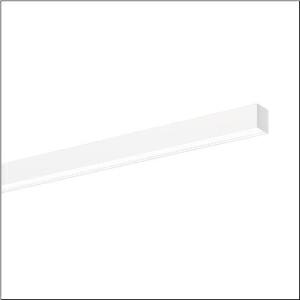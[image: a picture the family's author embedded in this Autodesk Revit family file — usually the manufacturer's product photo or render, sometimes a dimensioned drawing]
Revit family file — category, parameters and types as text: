
# Revit family: silica_r__21_51mx20da32wb_d50a
name_source: partatom
category: Lighting Fixtures
units: mm (PartAtom-declared; Revit-internal decimal feet)

## family parameters
Cut with Voids When Loaded = No
Host = Face
Light Source = No
Part Type = Normal
Room Calculation Point = No
Round Connector Dimension = Use Diameter
Shared = No

## types (1)
- --- (1 x LED, 2400 lm, 16.1 W, 3000K)
    Apparent Load = 16 VA
    CIE Flux Codes = 48 79 96 100 100
    Color Rendering = 80
    Color Temperature = 3000K
    Default Elevation = 1800 mm
    Description = Silica® 21, office luminaire, primary optical cover: cover, of PMMA, opal, light emission: direct distribution, primary light characteristic: symmetric, installation type: surface-mounted, LED, rated luminous flux: 2.400lm, luminous efficacy: 149lm/W, light colour: 830, colour temperature: 3000K, with terminal, 3+2-pole, max. 2.5mm², mains connection: 220..240V, AC, 50/60Hz, rated input power: 16.1W, luminaire housing, of aluminium, traffic white (RAL 9016), length: 1.204mm, width: 53mm, height: 53mm, protection rating (complete): IP20, insulation class (complete): insulation class I (protective earthing), certification: CE, permissible operating ambient temperature: 0..+35°C, standard: EN 50419, packaging unit: 1 piece
    Height = 0 mm  [stored 0 ft]
    Lamp = 1 x LED
    Lamp Light Flux = 2400 lm
    Lamp Power = 16.1 W
    Lamp count = 1
    Length = 1204 mm
    Luminous efficacy = 149 lm/W
    Manufacturer = Siteco
    ModVariant = No
    Model = 51MX20DA32WB
    Mounting Place = Ceiling
    Mounting Type = Recessed
    Number of Poles = 1
    OnlyDefault = Yes
    Power Factor = 1
    Product Name = Silica® 21
    Product group = office luminaire | ceiling recessed
    ProductGroupID = 401
    Protection Class = Protection class I
    Protection Degree = IP 20
    RLX_Detail_Level = 1
    RLX_Emergency_Light_Flux = 0 lm
    RLX_Emergency_Type = 0
    RLX_Emergency_Type_DB = No
    RlxData = <blob elided: 23825 chars, md5=f390351e>
    Socket = socket
    Standby Power = 0 W
    System Light Flux = 2400 lm
    System Power = 16 W
    Type Comments = factory setting: luminous flux: 100 % | dim-lin: 254 | 233 mA
    Type Image = l_1313601.jpg
    URL = http://relux.com
    VarID = @adj_066647
    Voltage = 0 V
    Weight = 0.00 kg
    Width = 53 mm

note: [stored X ft] marks values corroborated as IEEE doubles in the binary element streams (Revit-internal decimal feet)

## geometry (parser evidence)
native form markers: Blend x4, Sweep x10
no freeform markers — native parametric forms only
